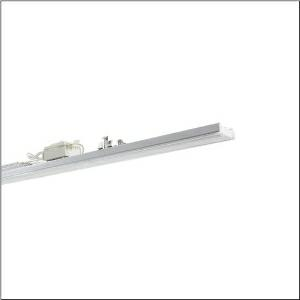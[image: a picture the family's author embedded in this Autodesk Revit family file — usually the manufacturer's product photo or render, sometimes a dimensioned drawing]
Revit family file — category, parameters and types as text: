
# Revit family: licross_21_recessed_ho_52tl1wcn4c5m
name_source: partatom
category: Lighting Fixtures
units: mm (PartAtom-declared; Revit-internal decimal feet)

## family parameters
Cut with Voids When Loaded = No
Host = Face
Light Source = No
Part Type = Normal
Room Calculation Point = No
Round Connector Dimension = Use Diameter
Shared = No

## types (1)
- --- (1 x LED, 12710 lm, 68.4 W, 4000K)
    Apparent Load = 68 VA
    CIE Flux Codes = 73 94 99 100 100
    Color Rendering = 80
    Color Temperature = 4000K
    Default Elevation = 1800 mm
    Description = Licross 21 Recessed HO, luminaire insert, of sheet steel, galvanised, coil coated, white, length: 1.500mm, width: 66mm, height: 67mm, LED rated luminous flux: 12.710lm, light colour: 840, SDCM (Standard Deviation of Colour Matching)MacAdam ≤ 3 SDCM (initial), control gear: ON/OFF Multilumen, CLOi, with plug, 3-pole, with phase selection, mains connection: 220..240V, AC, 50/60Hz, start of lifetime: 68W, end of service life: 83W, internal wiring halogen-free, primary optical cover: cover, of PMMA, light emission: direct distribution, primary light characteristic: symmetric, protection rating (complete): IP40, insulation class (complete): insulation class I (protective earthing), certification: CE, ENEC, VDE, UKCA, protection symbol: D if used in an environment without relevant dust loads with corresponding accessories, impact resistance: IK06, permissible ambient temperature for indoor applications: -35..+30°C, corresponds to IFS (International Featured Standards) requirements for safety and quality in the food industry, reducing of maximum allowable ambient temperature of 5°C with ceiling mounting, LABS conformity tested according to VDMA 24364:2018-05, The light source and the operating device comply with the requirements of the Ecodesign Regulation (EU) 2019/2020 and are replaceable in accordance with this regulation, packaging unit: 1 piece
    Height = 58 mm
    Lamp = 1 x LED
    Lamp Light Flux = 12710 lm
    Lamp Power = 68.4 W
    Lamp count = 1
    Length = 1500 mm
    Luminous efficacy = 186 lm/W
    Manufacturer = Siteco
    ModVariant = No
    Model = 52TL1WCN4C5M
    Mounting Place = Ceiling
    Mounting Type = Pendant
    Number of Poles = 1
    OnlyDefault = Yes
    Power Factor = 1
    Product Name = Licross 21 Recessed HO
    Product group = luminaire insert | ceiling pendant
    ProductGroupID = 901
    Protection Class = Protection class I
    Protection Degree = IP 40
    RLX_Detail_Level = 1
    RLX_Emergency_Light_Flux = 0 lm
    RLX_Emergency_Type = 0
    RLX_Emergency_Type_DB = No
    RlxData = <blob elided: 22601 chars, md5=35f14488>
    Socket = socket
    Standby Power = 0 W
    System Light Flux = 12710 lm
    System Power = 68 W
    Type Comments = factory setting: luminous flux: 100 % | (A | C | E) | 161 mA
    Type Image = l_1296930.jpg
    URL = http://relux.com
    VarID = @adj_066611
    Voltage = 0 V
    Weight = 0.00 kg
    Width = 66 mm

## geometry (parser evidence)
native form markers: Blend x4, Sweep x9
no freeform markers — native parametric forms only
